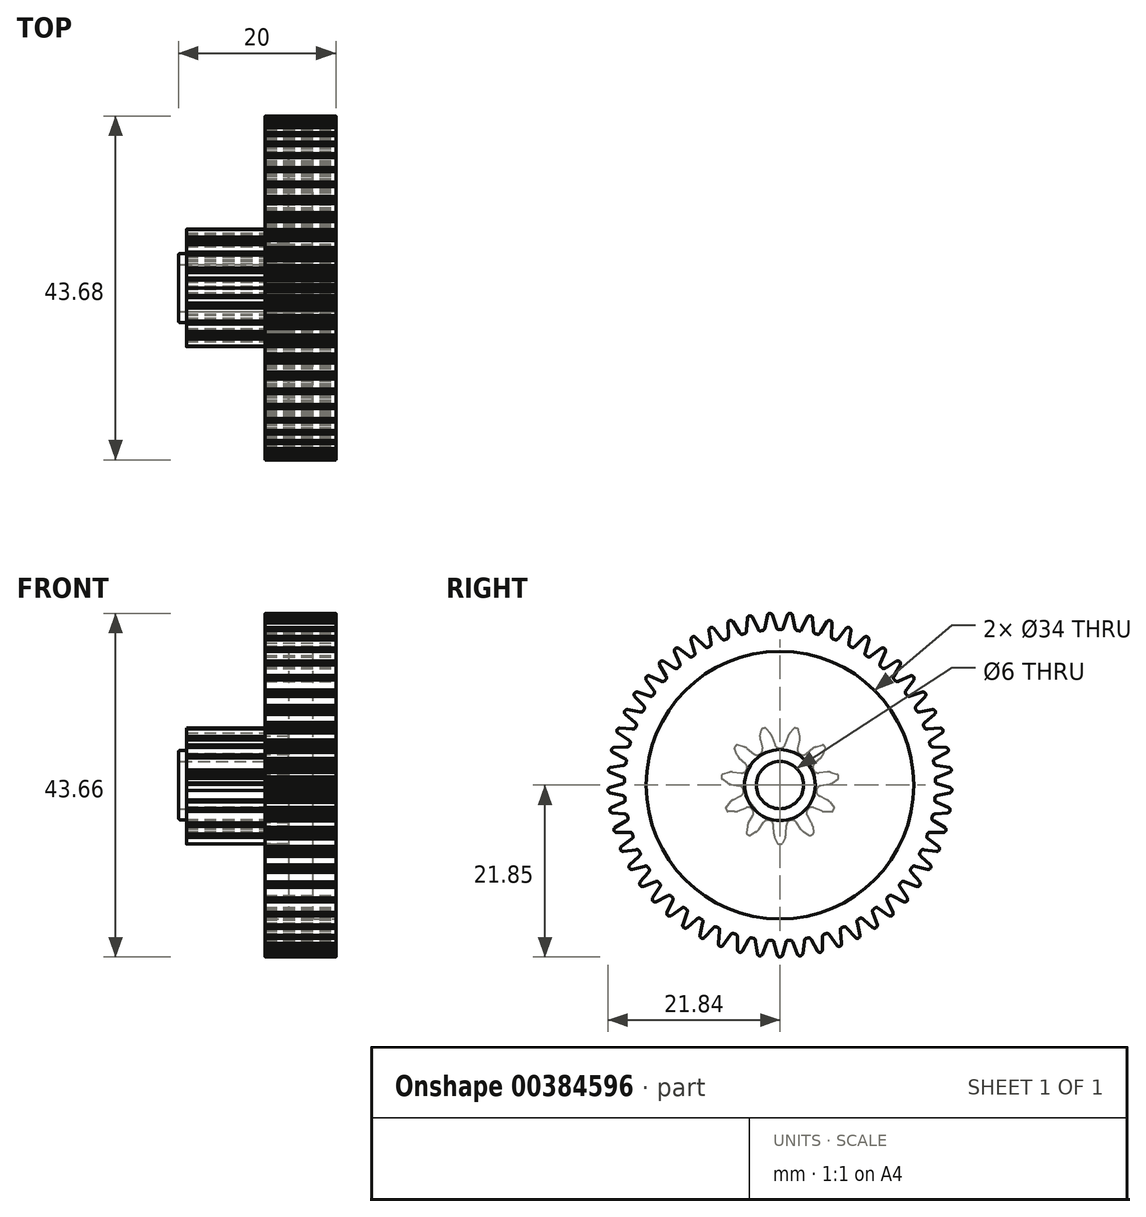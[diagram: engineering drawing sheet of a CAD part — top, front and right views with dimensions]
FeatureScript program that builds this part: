
annotation { "Feature Type Name" : "Feature", "Feature Type Description" : "" }
export const myFeature = defineFeature(function(context is Context, id is Id, definition is map)
    precondition{}
    {
        {
            var Q0;
            Q0=qCreatedBy(makeId("Front.planeOp"),FACE);
            var sketch = newSketch(context, id + "F0", { "sketchPlane" : qUnion([Q0])});
            skLineSegment(sketch, "E0.top", {"start": v(0, 21.85) * mm, "end": v(-9, 21.85) * mm});
            skLineSegment(sketch, "E0.left", {"start": v(0, 3) * mm, "end": v(0, 4.5) * mm});
            skLineSegment(sketch, "E0.right", {"start": v(-19, 4.4) * mm, "end": v(-19, 7.5) * mm});
            skLineSegment(sketch, "E1", {"start": v(0, 17) * mm, "end": v(-3, 17) * mm});
            skLineSegment(sketch, "E2", {"start": v(-3, 17) * mm, "end": v(-3, 4.5) * mm});
            skLineSegment(sketch, "E3", {"start": v(-3, 4.5) * mm, "end": v(0, 4.5) * mm});
            skLineSegment(sketch, "E4", {"start": v(-9, 21.85) * mm, "end": v(-9, 17) * mm});
            skLineSegment(sketch, "E5", {"start": v(-19, 3) * mm, "end": v(0, 3) * mm});
            skPoint(sketch, "E6.end.orphan", {"position": v(-19, 7.5) * mm});
            skLineSegment(sketch, "E7", {"start": v(-9, 17) * mm, "end": v(-6, 17) * mm});
            skLineSegment(sketch, "E8", {"start": v(-6, 17) * mm, "end": v(-6, 7.5) * mm});
            skLineSegment(sketch, "E9", {"start": v(-6, 7.5) * mm, "end": v(-19, 7.5) * mm});
            skLineSegment(sketch, "E10.trimOffspring", {"start": v(0, 17) * mm, "end": v(0, 21.85) * mm});
            skPoint(sketch, "E0.bottom.end.orphan", {"position": v(-19, 0) * mm});
            skPoint(sketch, "E0.bottom.start.orphan", {"position": v(0, 0) * mm});
            skLineSegment(sketch, "E11", {"start": v(25.3, 0) * mm, "end": v(-48.36, 0) * mm, "construction": true});
            skLineSegment(sketch, "E12", {"start": v(-19, 3) * mm, "end": v(-20, 3) * mm});
            skLineSegment(sketch, "E13", {"start": v(-20, 3) * mm, "end": v(-20, 4.4) * mm});
            skLineSegment(sketch, "E14", {"start": v(-20, 4.4) * mm, "end": v(-19, 4.4) * mm});
            skSolve(sketch);
        }
        {
            var Q0;
            Q0=makeQuery(id+"F0.imprint","IMPRINT",FACE,{"disambiguationData":[TD([[makeQuery(id+"F0.imprint","IMPRINT",EDGE,{"derivedFrom":sQuery(id+"F0.wireOp",EDGE,"E0.top")}),1.0]])]});
            var Q1;
            Q1=sQuery(id+"F0.wireOp",EDGE,"E11");
            revolve(context, id + "F1", {"entities" : qUnion([Q0]), "axis" : qUnion([Q1]), "revolveType" : RevolveType.FULL});
        }
        {
            var Q0;
            Q0=makeQuery(id+"F1.opRevolve","SWEPT_EDGE",EDGE,{"disambiguationData":[OSD([sQuery(id+"F0.wireOp",EDGE,"E0.left"),sQuery(id+"F0.wireOp",EDGE,"E5")])]});
            var Q1;
            Q1=makeQuery(id+"F1.opRevolve","SWEPT_EDGE",EDGE,{"disambiguationData":[OSD([sQuery(id+"F0.wireOp",EDGE,"E0.right"),sQuery(id+"F0.wireOp",EDGE,"E14")])]});
            var Q2;
            Q2=makeQuery(id+"F1.opRevolve","SWEPT_EDGE",EDGE,{"disambiguationData":[OSD([sQuery(id+"F0.wireOp",EDGE,"E0.left"),sQuery(id+"F0.wireOp",EDGE,"E5")])]});
            var Q3;
            Q3=makeQuery(id+"F1.opRevolve","SWEPT_EDGE",EDGE,{"disambiguationData":[OSD([sQuery(id+"F0.wireOp",EDGE,"E0.left"),sQuery(id+"F0.wireOp",EDGE,"E3")])]});
            var Q4;
            Q4=makeQuery(id+"F1.opRevolve","SWEPT_EDGE",EDGE,{"disambiguationData":[OSD([sQuery(id+"F0.wireOp",EDGE,"E1"),sQuery(id+"F0.wireOp",EDGE,"E2")])]});
            var Q5;
            Q5=makeQuery(id+"F1.opRevolve","SWEPT_EDGE",EDGE,{"disambiguationData":[OSD([sQuery(id+"F0.wireOp",EDGE,"E1"),sQuery(id+"F0.wireOp",EDGE,"E10.trimOffspring")])]});
            var Q6;
            Q6=makeQuery(id+"F1.opRevolve","SWEPT_EDGE",EDGE,{"disambiguationData":[OSD([sQuery(id+"F0.wireOp",EDGE,"E7"),sQuery(id+"F0.wireOp",EDGE,"E8")])]});
            var Q7;
            Q7=makeQuery(id+"F1.opRevolve","SWEPT_EDGE",EDGE,{"disambiguationData":[OSD([sQuery(id+"F0.wireOp",EDGE,"E4"),sQuery(id+"F0.wireOp",EDGE,"E7")])]});
            var Q8;
            Q8=makeQuery(id+"F1.opRevolve","SWEPT_EDGE",EDGE,{"disambiguationData":[OSD([sQuery(id+"F0.wireOp",EDGE,"E13"),sQuery(id+"F0.wireOp",EDGE,"E14")])]});
            var Q9;
            Q9=makeQuery(id+"F1.opRevolve","SWEPT_EDGE",EDGE,{"disambiguationData":[OSD([sQuery(id+"F0.wireOp",EDGE,"E12"),sQuery(id+"F0.wireOp",EDGE,"E13")])]});
            var Q10;
            Q10=makeQuery(id+"F1.opRevolve","SWEPT_EDGE",EDGE,{"disambiguationData":[OSD([sQuery(id+"F0.wireOp",EDGE,"E2"),sQuery(id+"F0.wireOp",EDGE,"E3")])]});
            fillet(context, id + "F2", {"entities" : qUnion([Q0, Q1, Q2, Q3, Q4, Q5, Q6, Q7, Q8, Q9, Q10]), "radius" : 0.2 * mm, "allowEdgeOverflow" : false});
        }
        {
            var Q0;
            Q0=makeQuery(id+"F1.opRevolve","SWEPT_FACE",FACE,{"disambiguationData":[OSD([sQuery(id+"F0.wireOp",EDGE,"E0.right")])]});
            var sketch = newSketch(context, id + "F3", { "sketchPlane" : qUnion([Q0])});
            skLineSegment(sketch, "E15", {"start": v(0, 0) * mm, "end": v(0, 8.63) * mm, "construction": true});
            skPoint(sketch, "E16.trimOffspring.end.orphan", {"position": v(1.2, 7.4) * mm});
            skLineSegment(sketch, "E17.trimOffspring", {"start": v(0, 0) * mm, "end": v(0, -1.33) * mm, "construction": true});
            skPoint(sketch, "E18.start.orphan", {"position": v(0, 7.5) * mm});
            skPoint(sketch, "E19.visualSharp", {"position": v(-0.82, 4.89) * mm});
            skPoint(sketch, "E20.visualSharp", {"position": v(0.37, 4.84) * mm});
            skArc(sketch, "E20.filletArc", {"start": v(-0.01, 4.86) * mm, "mid": v(0, 4.86) * mm, "end": v(0, 4.86) * mm});
            skPoint(sketch, "E21.orphan", {"position": v(-1.2, 7.4) * mm});
            skPoint(sketch, "E22.orphan", {"position": v(0.9, 6.47) * mm});
            skPoint(sketch, "E23.orphan", {"position": v(0.7, 5.84) * mm});
            skPoint(sketch, "E24.orphan", {"position": v(1.28, 6.9) * mm});
            skPoint(sketch, "E25.MirrorCS.start.orphan", {"position": v(-1.06, 6.47) * mm});
            skLineSegment(sketch, "E26.0", {"start": v(1.23, 6.57) * mm, "end": v(1.8, 7.2) * mm});
            skArc(sketch, "E26.1", {"start": v(1.23, 6.57) * mm, "mid": v(1.1, 6.38) * mm, "end": v(1, 6.18) * mm});
            skLineSegment(sketch, "E26.2", {"start": v(1, 6.18) * mm, "end": v(0.66, 5.15) * mm});
            skArc(sketch, "E26.3", {"start": v(-0.02, 4.68) * mm, "mid": v(0.4, 4.8) * mm, "end": v(0.66, 5.15) * mm});
            skArc(sketch, "E27", {"start": v(1.93, 7.25) * mm, "mid": v(1.86, 7.23) * mm, "end": v(1.8, 7.2) * mm});
            skPoint(sketch, "E28.orphan", {"position": v(1.67, 7.31) * mm});
            skPoint(sketch, "E29.orphan", {"position": v(0.48, 5.2) * mm});
            skArc(sketch, "E30.MirrorCS", {"start": v(0.02, 4.68) * mm, "mid": v(-0.4, 4.8) * mm, "end": v(-0.66, 5.15) * mm});
            skLineSegment(sketch, "E31.MirrorCS", {"start": v(-1, 6.18) * mm, "end": v(-0.66, 5.15) * mm});
            skArc(sketch, "E32.MirrorCS", {"start": v(-1.23, 6.57) * mm, "mid": v(-1.1, 6.38) * mm, "end": v(-1, 6.18) * mm});
            skLineSegment(sketch, "E33.MirrorCS", {"start": v(-1.23, 6.57) * mm, "end": v(-1.8, 7.2) * mm});
            skArc(sketch, "E34.MirrorCS", {"start": v(-1.93, 7.25) * mm, "mid": v(-1.86, 7.23) * mm, "end": v(-1.8, 7.2) * mm});
            skSolve(sketch);
        }
        {
            var Q0;
            Q0=makeQuery(id+"F3.imprint","IMPRINT",FACE,{"disambiguationData":[TD([[makeQuery(id+"F3.imprint","IMPRINT",EDGE,{"derivedFrom":sQuery(id+"F3.wireOp",EDGE,"E26.0")}),1.0]])]});
            extrude(context, id + "F4", {"entities" : qUnion([Q0]), "operationType" : NewBodyOperationType.REMOVE, "oppositeDirection" : true, "offsetDistance" : 25 * mm, "depth" : 13 * mm});
        }
        {
            var Q0;
            Q0=makeQuery(id+"F4.boolean.opBoolean","COPY",FACE,{"derivedFrom":makeQuery(id+"F4.opExtrude","SWEPT_FACE",FACE,{"disambiguationData":[OSD([sQuery(id+"F3.wireOp",EDGE,"E34.MirrorCS")])]})});
            var Q1;
            Q1=makeQuery(id+"F4.boolean.opBoolean","COPY",FACE,{"derivedFrom":makeQuery(id+"F4.opExtrude","SWEPT_FACE",FACE,{"disambiguationData":[OSD([sQuery(id+"F3.wireOp",EDGE,"E33.MirrorCS")])]})});
            var Q2;
            Q2=makeQuery(id+"F4.boolean.opBoolean","COPY",FACE,{"derivedFrom":makeQuery(id+"F4.opExtrude","SWEPT_FACE",FACE,{"disambiguationData":[OSD([sQuery(id+"F3.wireOp",EDGE,"E32.MirrorCS")])]})});
            var Q3;
            Q3=makeQuery(id+"F4.boolean.opBoolean","COPY",FACE,{"derivedFrom":makeQuery(id+"F4.opExtrude","SWEPT_FACE",FACE,{"disambiguationData":[OSD([sQuery(id+"F3.wireOp",EDGE,"E31.MirrorCS")])]})});
            var Q4;
            Q4=makeQuery(id+"F4.boolean.opBoolean","COPY",FACE,{"derivedFrom":makeQuery(id+"F4.opExtrude","SWEPT_FACE",FACE,{"disambiguationData":[OSD([sQuery(id+"F3.wireOp",EDGE,"E30.MirrorCS")])]})});
            var Q5;
            Q5=makeQuery(id+"F4.boolean.opBoolean","COPY",FACE,{"derivedFrom":makeQuery(id+"F4.opExtrude","SWEPT_FACE",FACE,{"disambiguationData":[OSD([sQuery(id+"F3.wireOp",EDGE,"E26.3")])]})});
            var Q6;
            Q6=makeQuery(id+"F4.boolean.opBoolean","COPY",FACE,{"derivedFrom":makeQuery(id+"F4.opExtrude","SWEPT_FACE",FACE,{"disambiguationData":[OSD([sQuery(id+"F3.wireOp",EDGE,"E26.2")])]})});
            var Q7;
            Q7=makeQuery(id+"F4.boolean.opBoolean","COPY",FACE,{"derivedFrom":makeQuery(id+"F4.opExtrude","SWEPT_FACE",FACE,{"disambiguationData":[OSD([sQuery(id+"F3.wireOp",EDGE,"E26.1")])]})});
            var Q8;
            Q8=makeQuery(id+"F4.boolean.opBoolean","COPY",FACE,{"derivedFrom":makeQuery(id+"F4.opExtrude","SWEPT_FACE",FACE,{"disambiguationData":[OSD([sQuery(id+"F3.wireOp",EDGE,"E26.0")])]})});
            var Q9;
            Q9=makeQuery(id+"F4.boolean.opBoolean","COPY",FACE,{"derivedFrom":makeQuery(id+"F4.opExtrude","SWEPT_FACE",FACE,{"disambiguationData":[OSD([sQuery(id+"F3.wireOp",EDGE,"E27")])]})});
            var Q10;
            Q10=makeQuery(id+"F1.opRevolve","SWEPT_FACE",FACE,{"disambiguationData":[OSD([sQuery(id+"F0.wireOp",EDGE,"E9")])]});
            circularPattern(context, id + "F5", {"patternType" : PatternType.FACE, "faces" : qUnion([Q0, Q1, Q2, Q3, Q4, Q5, Q6, Q7, Q8, Q9]), "axis" : qUnion([Q10]), "angle" : 360 * degree, "instanceCount" : 11, "oppositeDirection" : true, "equalSpace" : true, "fullFeaturePattern" : false});
        }
        {
            var Q0;
            Q0=makeQuery(id+"F1.opRevolve","SWEPT_FACE",FACE,{"disambiguationData":[OSD([sQuery(id+"F0.wireOp",EDGE,"E10.trimOffspring")])]});
            var sketch = newSketch(context, id + "F6", { "sketchPlane" : qUnion([Q0])});
            skCircle(sketch, "E35", {"center": v(0, 0) * mm, "radius": 19.75 * mm});
            skLineSegment(sketch, "E36", {"start": v(0, 19.75) * mm, "end": v(0.4, 19.75) * mm, "construction": true});
            skArc(sketch, "E37", {"start": v(0.2, 19.75) * mm, "mid": v(0.37, 19.87) * mm, "end": v(0.45, 20.06) * mm});
            skArc(sketch, "E38", {"start": v(1.25, 21.81) * mm, "mid": v(1.07, 21.74) * mm, "end": v(0.95, 21.6) * mm});
            skLineSegment(sketch, "E39", {"start": v(0.2, 19.75) * mm, "end": v(0, 19.75) * mm});
            skLineSegment(sketch, "E40", {"start": v(0.45, 20.06) * mm, "end": v(0.95, 21.6) * mm});
            skArc(sketch, "E41.MirrorCS", {"start": v(-1.25, 21.81) * mm, "mid": v(-1.07, 21.74) * mm, "end": v(-0.95, 21.6) * mm});
            skLineSegment(sketch, "E42.MirrorCS", {"start": v(-0.45, 20.06) * mm, "end": v(-0.95, 21.6) * mm});
            skArc(sketch, "E43.MirrorCS", {"start": v(-0.2, 19.75) * mm, "mid": v(-0.37, 19.87) * mm, "end": v(-0.45, 20.06) * mm});
            skLineSegment(sketch, "E44.MirrorCS", {"start": v(0, 19.75) * mm, "end": v(-0.4, 19.75) * mm, "construction": true});
            skLineSegment(sketch, "E45", {"start": v(-0.2, 19.75) * mm, "end": v(0.2, 19.75) * mm});
            skSolve(sketch);
        }
        {
            var Q0;
            {var subQ4=sQuery(id+"F6.wireOp",EDGE,"E38");Q0=makeQuery(id+"F6.imprint","IMPRINT",FACE,{"disambiguationData":[TD([[makeQuery(id+"F6.imprint","IMPRINT",EDGE,{"derivedFrom":subQ4}),-1.0]])]});}
            extrude(context, id + "F7", {"entities" : qUnion([Q0]), "operationType" : NewBodyOperationType.REMOVE, "flatOperationType" : FlatOperationType.REMOVE, "oppositeDirection" : true, "offsetDistance" : 25 * mm, "depth" : 9 * mm, "domain" : OperationDomain.MODEL});
        }
        {
            var Q0;
            Q0=makeQuery(id+"F7.boolean.opBoolean","COPY",FACE,{"derivedFrom":makeQuery(id+"F7.opExtrude","SWEPT_FACE",FACE,{"disambiguationData":[OSD([sQuery(id+"F6.wireOp",EDGE,"E42.MirrorCS")])]})});
            var Q1;
            Q1=makeQuery(id+"F7.boolean.opBoolean","COPY",FACE,{"derivedFrom":makeQuery(id+"F7.opExtrude","SWEPT_FACE",FACE,{"disambiguationData":[OSD([sQuery(id+"F6.wireOp",EDGE,"E41.MirrorCS")])]})});
            var Q2;
            Q2=makeQuery(id+"F7.boolean.opBoolean","COPY",FACE,{"derivedFrom":makeQuery(id+"F7.opExtrude","SWEPT_FACE",FACE,{"disambiguationData":[OSD([sQuery(id+"F6.wireOp",EDGE,"E43.MirrorCS")])]})});
            var Q3;
            Q3=makeQuery(id+"F7.boolean.opBoolean","COPY",FACE,{"derivedFrom":makeQuery(id+"F7.opExtrude","SWEPT_FACE",FACE,{"disambiguationData":[OSD([sQuery(id+"F6.wireOp",EDGE,"E35")])]})});
            var Q4;
            Q4=makeQuery(id+"F7.boolean.opBoolean","COPY",FACE,{"derivedFrom":makeQuery(id+"F7.opExtrude","SWEPT_FACE",FACE,{"disambiguationData":[OSD([sQuery(id+"F6.wireOp",EDGE,"E37")])]})});
            var Q5;
            Q5=makeQuery(id+"F7.boolean.opBoolean","COPY",FACE,{"derivedFrom":makeQuery(id+"F7.opExtrude","SWEPT_FACE",FACE,{"disambiguationData":[OSD([sQuery(id+"F6.wireOp",EDGE,"E40")])]})});
            var Q6;
            Q6=makeQuery(id+"F7.boolean.opBoolean","COPY",FACE,{"derivedFrom":makeQuery(id+"F7.opExtrude","SWEPT_FACE",FACE,{"disambiguationData":[OSD([sQuery(id+"F6.wireOp",EDGE,"E38")])]})});
            var Q7;
            Q7=makeQuery(id+"F1.opRevolve","SWEPT_FACE",FACE,{"disambiguationData":[OSD([sQuery(id+"F0.wireOp",EDGE,"E0.top")])]});
            circularPattern(context, id + "F8", {"patternType" : PatternType.FACE, "faces" : qUnion([Q0, Q1, Q2, Q3, Q4, Q5, Q6]), "axis" : qUnion([Q7]), "angle" : 360 * degree, "instanceCount" : 53, "oppositeDirection" : true, "equalSpace" : true});
        }
    });
